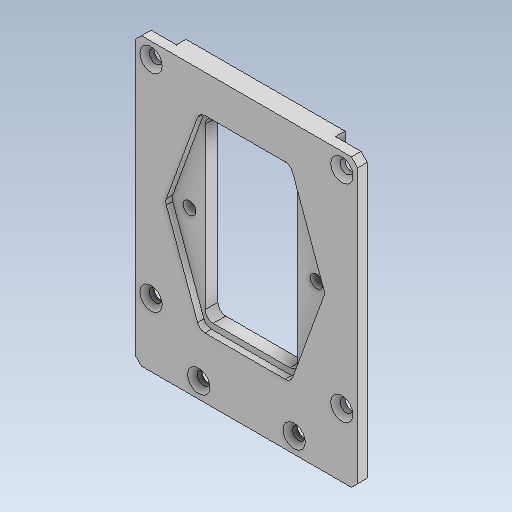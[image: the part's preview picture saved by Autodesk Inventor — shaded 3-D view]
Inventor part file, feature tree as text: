
AUTODESK INVENTOR PART (.ipt)
format: ipt  version: 2020 (Build 240168000, 168)  size: 301,568 bytes
history: native  units: mm
features: sketch x8, extrude x7, hole x2, reference x2, other x2, fillet x1, chamfer x1, projected_geometry x1
ambient origin geometry x8: Origin, YZ Plane, XZ Plane, XY Plane, X Axis, Y Axis, Z Axis, Center Point
bodies: Solid1 (feature_tree)
feature tree (24):
  extrude  "Extrusion1"  Depth=90.0mm
  extrude  "Extrusion2"  TaperAngle=0.0deg  [1 undecoded]
  extrude  "Extrusion3"  Depth=15.0mm
  extrude  "Extrusion4"  Depth=20.0mm
  hole  "Hole1"  [1 undecoded]
  extrude  "Extrusion5"  TaperAngle=0.0deg  [1 undecoded]
  extrude  "Extrusion6"  Depth=10.0mm
  extrude  "Extrusion7"  Depth=20.0mm
  fillet  "Fillet1"  Radius=20.0mm
  hole  "Hole4"  [1 undecoded]
  chamfer  "Chamfer2"  Distance=5.0mm
  sketch  "Sketch1"  dims[d0=70.0mm d1=90.0mm]
  sketch  "Sketch2"  dims[d2=23.0mm d3=0.0mm d5=0.0mm d6=0.0mm]
  sketch  "Sketch3"  dims[d8=2.0mm d9=0.0mm d11=15.0mm]
  sketch  "Sketch4"  dims[d14=20.0mm d15=0.0mm d17=5.0mm]
  sketch  "Sketch5"  dims[d23=17.0mm d24=0.0mm]
  sketch  "Sketch6"  dims[d25=4.0mm d26=6.0mm d27=4.0mm d28=2.0mm d29=90.0deg d30=8.0mm d31=20.594885mm d35=5.0mm]
  reference  "Reference1"
  reference  "Reference2"
  projected_geometry  "Projected Loop1"
  sketch  "Sketch10"  dims[d55=30.0mm d56=0.0mm d62=0.0mm d63=0.0mm]
  sketch  "Sketch11"  dims[d64=0.5mm d65=5.0mm d66=20.0mm d67=20.0mm d68=5.0mm d69=5.0mm d70=20.0mm d71=5.0mm d72=5.0mm d73=4.0mm d74=6.0mm d75=7.0mm d76=2.0mm d77=90.0deg d78=8.0mm d79=20.594885mm d80=30.0mm d84=2.0mm d85=2.0mm d86=45.0deg d89=10.0mm d90=0.5mm d91=0.5mm d94=10.0mm d96=20.092775mm d97=5.0mm]
  other  "Ansamblu nconector priza.iam"
  other  "0008-20-1006 Inlet Module Plug Fuse Switch Male Power Socket 10A 250V 3 Pin IEC320 C14:1"
note: 4 required parameter values undecoded (feature->parameter linkage not recoverable at this tier; creation-order binding heuristic only, values carry confidence <= 0.55)
